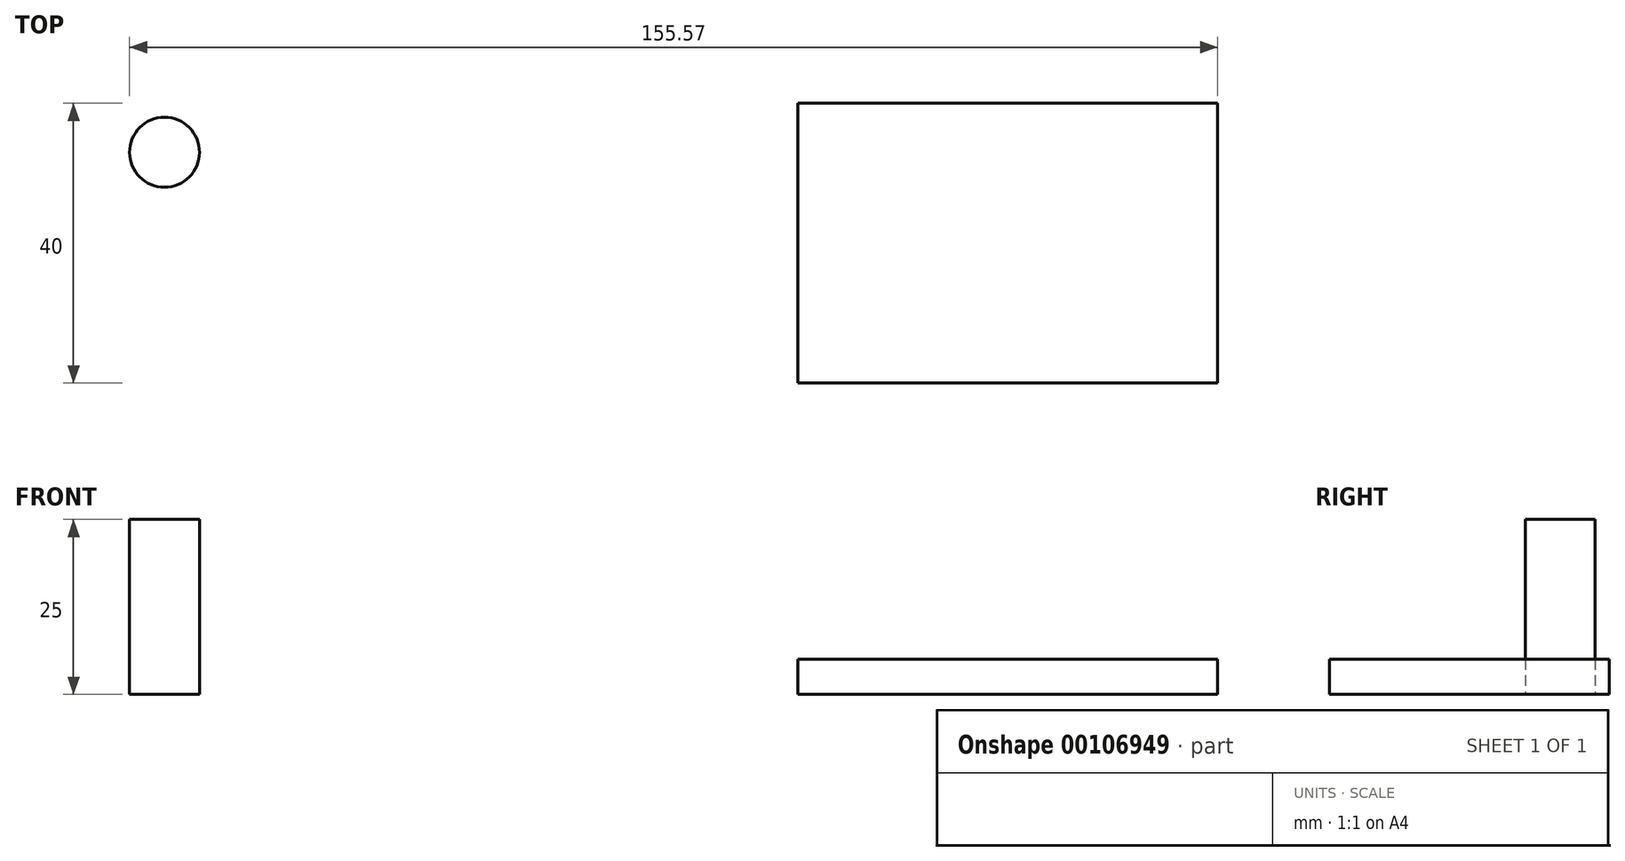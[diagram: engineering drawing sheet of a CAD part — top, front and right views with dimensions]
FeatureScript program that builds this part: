
annotation { "Feature Type Name" : "Feature", "Feature Type Description" : "" }
export const myFeature = defineFeature(function(context is Context, id is Id, definition is map)
    precondition{}
    {
        {
            var Q0;
            Q0=qCreatedBy(makeId("Top.planeOp"),FACE);
            var sketch = newSketch(context, id + "F0", { "sketchPlane" : qUnion([Q0])});
            skLineSegment(sketch, "E0.rect.bottom", {"start": v(30, 20) * mm, "end": v(-30, 20) * mm});
            skLineSegment(sketch, "E0.rect.top", {"start": v(30, -20) * mm, "end": v(-30, -20) * mm});
            skLineSegment(sketch, "E0.rect.left", {"start": v(30, 20) * mm, "end": v(30, -20) * mm});
            skLineSegment(sketch, "E0.rect.right", {"start": v(-30, 20) * mm, "end": v(-30, -20) * mm});
            skPoint(sketch, "E0.rect.middle", {"position": v(0, 0) * mm});
            skCircle(sketch, "E1", {"center": v(-120.57, 12.99) * mm, "radius": 5 * mm});
            skSolve(sketch);
        }
        {
            var Q0;
            Q0=makeQuery(id+"F0.imprint","IMPRINT",FACE,{"disambiguationData":[TD([[makeQuery(id+"F0.imprint","IMPRINT",EDGE,{"derivedFrom":sQuery(id+"F0.wireOp",EDGE,"E0.rect.bottom")}),1.0]])]});
            extrude(context, id + "F1", {"entities" : qUnion([Q0]), "depth" : 5 * mm});
        }
        {
            var Q0;
            Q0=makeQuery(id+"F0.imprint","IMPRINT",FACE,{"disambiguationData":[TD([[makeQuery(id+"F0.imprint","IMPRINT",EDGE,{"derivedFrom":sQuery(id+"F0.wireOp",EDGE,"E1")}),1.0]])]});
            extrude(context, id + "F2", {"entities" : qUnion([Q0]), "depth" : 25 * mm});
        }
    });
